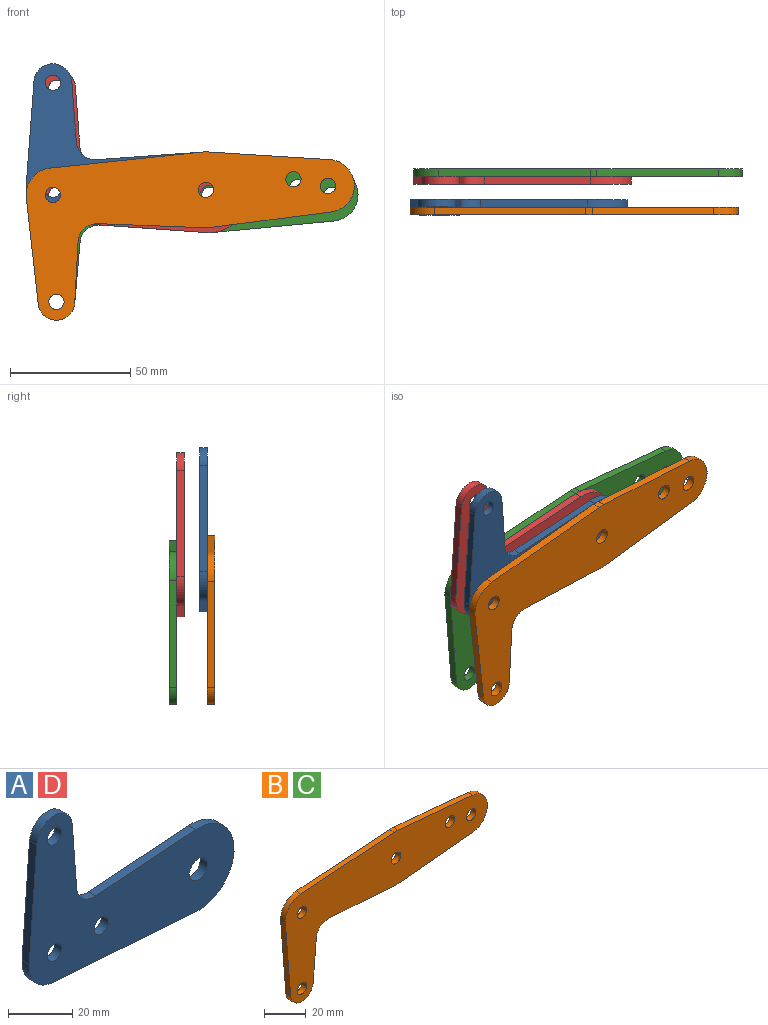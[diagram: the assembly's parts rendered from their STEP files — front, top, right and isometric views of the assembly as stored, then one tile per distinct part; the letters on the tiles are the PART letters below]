
ASSEMBLY  parts=4 mates=3
PART A: 14 faces, bbox 90.4x3.2x68.1 mm
  f0: plane 44.2x3.29mm, normal (-1,0,0.07), area 140.7mm2, adj f1,f10,f12,f13
  f1: cylinder r=11.18mm len=11.98mm, axis (0,1,0), area 55.8mm2, adj f0,f2,f12,f13
  f2: plane 63.17x4.56mm, normal (-0.07,0,-1), area 201.1mm2, adj f1,f3,f12,f13
  f3: cylinder r=15.75mm len=31.5mm, axis (0,1,0), area 164.3mm2, adj f2,f4,f12,f13
  f4: plane 44.21x3.19mm, normal (-0.07,0,1), area 140.7mm2, adj f3,f5,f12,f13
  f5: cylinder r=7.87mm len=8.42mm, axis (0,1,0), area 39.2mm2, adj f4,f6,f12,f13
  f6: plane 25.25x3.18mm, normal (1,0,0.07), area 80.4mm2, adj f5,f10,f12,f13
  f7: cylinder r=3.17mm len=6.35mm, axis (0,1,0), area 63.3mm2, adj f12,f13
  f8: cylinder r=3.17mm len=6.35mm, axis (0,1,0), area 63.3mm2, adj f12,f13
  f9: cylinder r=3.17mm len=6.35mm, axis (0,1,0), area 63.3mm2, adj f12,f13
  f10: cylinder r=7.87mm len=15.7mm, axis (0,1,0), area 74.8mm2, adj f0,f6,f12,f13
  f11: cylinder r=3.98mm len=7.95mm, axis (0,1,0), area 79.3mm2, adj f12,f13
  f12: plane 90.42x68.07mm, normal (0,-1,0), area 2892.1mm2, adj f0,f1,f2,f3,f4,f5,f6,f7
  f13: plane 90.42x68.07mm, normal (0,1,0), area 2892.1mm2, adj f0,f1,f2,f3,f4,f5,f6,f7
PART B: 19 faces, bbox 136.4x3.2x67.8 mm
  f0: plane 50.34x4.8mm, normal (0.1,0,1), area 160.6mm2, adj f1,f16,f17,f18
  f1: cylinder r=15.75mm len=3.18mm, axis (0,1,0), area 8.4mm2, adj f0,f2,f17,f18
  f2: plane 63.17x4.56mm, normal (-0.07,0,1), area 201.1mm2, adj f1,f3,f17,f18
  f3: cylinder r=11.18mm len=12.04mm, axis (0,1,0), area 56mm2, adj f2,f4,f17,f18
  f4: plane 44.17x3.54mm, normal (-1,0,-0.08), area 140.7mm2, adj f3,f5,f17,f18
  f5: cylinder r=7.62mm len=15.19mm, axis (0,1,0), area 72mm2, adj f4,f6,f17,f18
  f6: plane 25.36x3.18mm, normal (1,0,-0.09), area 80.8mm2, adj f5,f7,f17,f18
  f7: cylinder r=7.87mm len=8.4mm, axis (0,1,0), area 38.9mm2, adj f6,f8,f17,f18
  f8: plane 44.2x3.18mm, normal (-0.07,0,-1), area 140.7mm2, adj f7,f9,f17,f18
  f9: cylinder r=15.75mm len=3.18mm, axis (0,1,0), area 8.3mm2, adj f8,f10,f17,f18
  f10: plane 50.34x4.8mm, normal (0.1,0,-1), area 160.6mm2, adj f9,f16,f17,f18
  f11: cylinder r=3.17mm len=6.35mm, axis (0,1,0), area 63.3mm2, adj f17,f18
  f12: cylinder r=3.17mm len=6.35mm, axis (0,1,0), area 63.3mm2, adj f17,f18
  f13: cylinder r=3.17mm len=6.35mm, axis (0,1,0), area 63.3mm2, adj f17,f18
  f14: cylinder r=3.17mm len=6.35mm, axis (0,1,0), area 63.3mm2, adj f17,f18
  f15: cylinder r=3.17mm len=6.35mm, axis (0,1,0), area 63.3mm2, adj f17,f18
  f16: cylinder r=10.92mm len=21.75mm, axis (0,1,0), area 102.3mm2, adj f0,f10,f17,f18
  f17: plane 136.4x67.82mm, normal (0,-1,0), area 4024.9mm2, adj f0,f1,f2,f3,f4,f5,f6,f7
  f18: plane 136.4x67.82mm, normal (0,1,0), area 4024.9mm2, adj f0,f1,f2,f3,f4,f5,f6,f7
PART C: same geometry as B
PART D: same geometry as A
PLACE A t=(31.32,-2.53,36.86)mm
PLACE B rot(axis=(0,-1,0),1.9deg) t=(31.35,-5.7,34.79)mm
PLACE C t=(32.8,10.17,34.82)mm
PLACE D t=(32.8,7,34.82)mm
MATE revolute D.f11 <-> C.f9  axis (0,1,0) through (96.3,8.59,34.82)mm
MATE cylindrical B.f11 <-> C.f11  axis (0,-1,0) through (32.8,-7.29,-9.63)mm
MATE revolute A.f3 <-> B.f13  axis (0,-1,0) through (94.82,-4.11,36.86)mm
